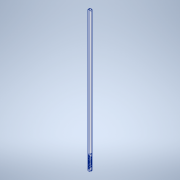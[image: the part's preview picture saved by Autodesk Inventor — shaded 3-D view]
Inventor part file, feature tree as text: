
AUTODESK INVENTOR PART (.ipt)
format: ipt  version: 2020.3 (Build 243373000, 373)  size: 193,536 bytes
history: native  units: mm
features: sketch x7, hole x6, other x1, extrude x1
ambient origin geometry x8: Origin, YZ Plane, XZ Plane, XY Plane, X Axis, Y Axis, Z Axis, Center Point
bodies: Body1 (feature_tree)
feature tree (15):
  other  "ソリッド1"
  extrude  "押し出し1"  Depth=15.0mm
  hole  "穴1"  [1 undecoded]
  hole  "穴2"  [1 undecoded]
  hole  "穴3"  [1 undecoded]
  hole  "穴4"  [1 undecoded]
  hole  "穴5"  [1 undecoded]
  hole  "穴6"  [1 undecoded]
  sketch  "スケッチ1"
  sketch  "スケッチ3"
  sketch  "スケッチ4"
  sketch  "スケッチ5"
  sketch  "スケッチ6"
  sketch  "スケッチ7"
  sketch  "スケッチ8"
note: 6 required parameter values undecoded (feature->parameter linkage not recoverable at this tier; creation-order binding heuristic only, values carry confidence <= 0.55)
